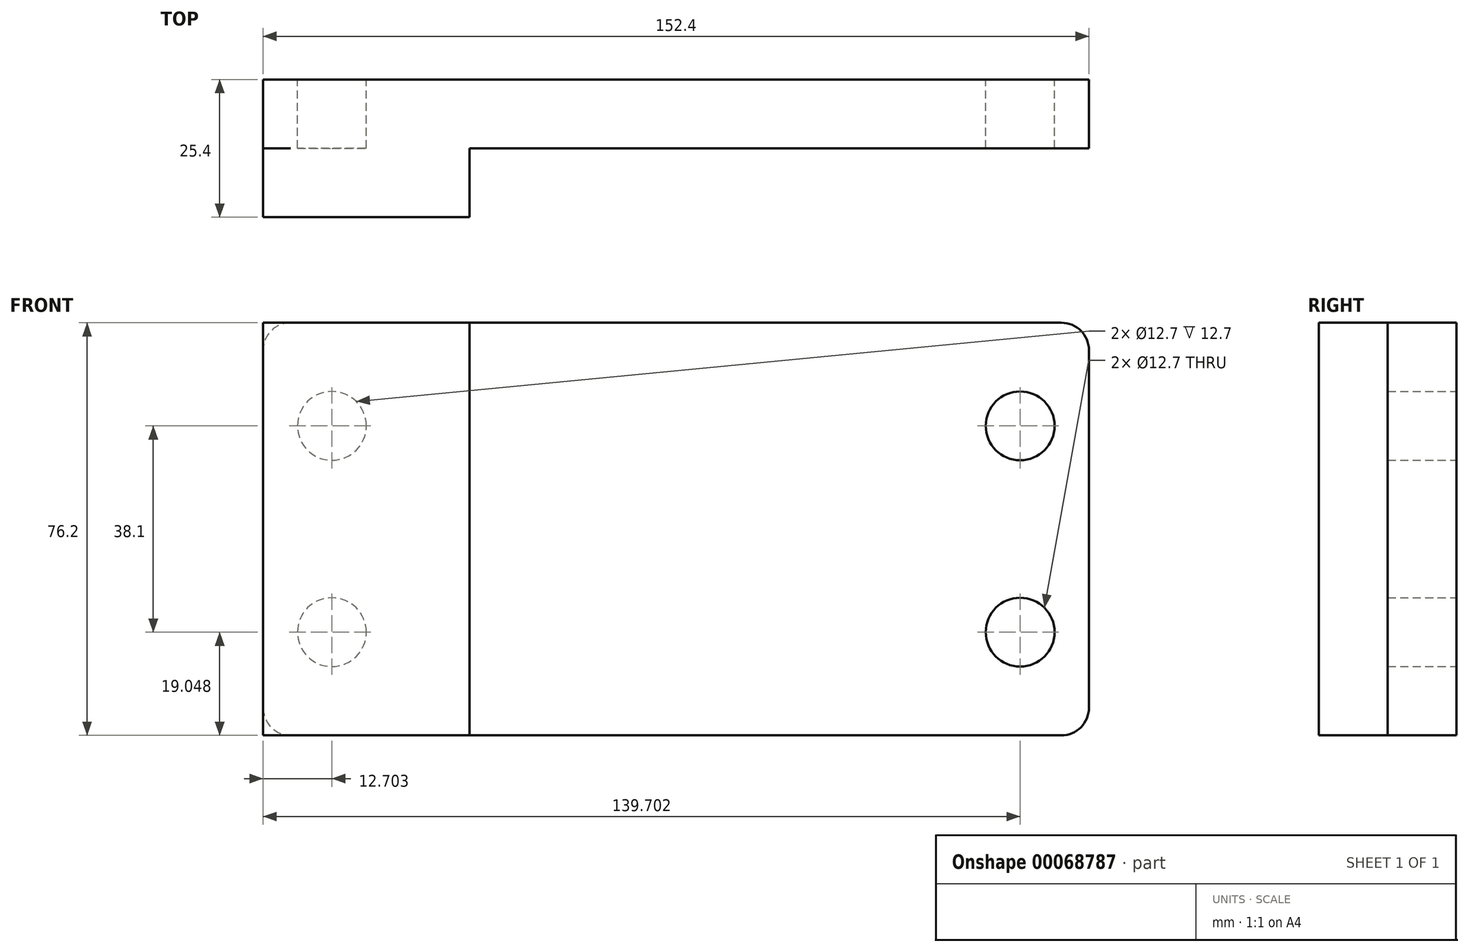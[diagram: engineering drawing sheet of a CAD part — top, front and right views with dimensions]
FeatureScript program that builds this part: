
annotation { "Feature Type Name" : "Feature", "Feature Type Description" : "" }
export const myFeature = defineFeature(function(context is Context, id is Id, definition is map)
    precondition{}
    {
        {
            var Q0;
            Q0=qCreatedBy(makeId("Front.planeOp"),FACE);
            var sketch = newSketch(context, id + "F0", { "sketchPlane" : qUnion([Q0])});
            skLineSegment(sketch, "E0.bottom", {"start": v(-76.72, 31.36) * mm, "end": v(75.68, 31.36) * mm});
            skLineSegment(sketch, "E0.top", {"start": v(-76.72, -44.84) * mm, "end": v(75.68, -44.84) * mm});
            skLineSegment(sketch, "E0.left", {"start": v(-76.72, 31.36) * mm, "end": v(-76.72, -44.84) * mm});
            skLineSegment(sketch, "E0.right", {"start": v(75.68, 31.36) * mm, "end": v(75.68, -44.84) * mm});
            skCircle(sketch, "E1", {"center": v(-64.02, 12.3) * mm, "radius": 6.35 * mm});
            skLineSegment(sketch, "E2.MirrorCS", {"start": v(76.72, 31.36) * mm, "end": v(76.72, -44.84) * mm});
            skLineSegment(sketch, "E3", {"start": v(-0.52, 31.36) * mm, "end": v(-0.52, -44.84) * mm, "construction": true});
            skCircle(sketch, "E4.MirrorC", {"center": v(62.98, 12.3) * mm, "radius": 6.35 * mm});
            skLineSegment(sketch, "E5", {"start": v(-76.72, -6.74) * mm, "end": v(75.68, -6.74) * mm, "construction": true});
            skCircle(sketch, "E6.MirrorC", {"center": v(62.98, -25.8) * mm, "radius": 6.35 * mm});
            skCircle(sketch, "E7.MirrorC", {"center": v(-64.02, -25.8) * mm, "radius": 6.35 * mm});
            skSolve(sketch);
        }
        {
            var Q0;
            Q0=makeQuery(id+"F0.imprint","IMPRINT",FACE,{"disambiguationData":[TD([[makeQuery(id+"F0.imprint","IMPRINT",EDGE,{"derivedFrom":sQuery(id+"F0.wireOp",EDGE,"E0.bottom")}),-1.0]])]});
            extrude(context, id + "F1", {"entities" : qUnion([Q0]), "depth" : 12.7 * mm});
        }
        {
            var Q0;
            Q0=makeQuery(id+"F1.opExtrude","SWEPT_EDGE",EDGE,{"disambiguationData":[OSD([sQuery(id+"F0.wireOp",EDGE,"E0.bottom"),sQuery(id+"F0.wireOp",EDGE,"E0.left")])]});
            var Q1;
            Q1=makeQuery(id+"F1.opExtrude","SWEPT_EDGE",EDGE,{"disambiguationData":[OSD([sQuery(id+"F0.wireOp",EDGE,"E0.top"),sQuery(id+"F0.wireOp",EDGE,"E0.left")])]});
            var Q2;
            Q2=makeQuery(id+"F1.opExtrude","SWEPT_EDGE",EDGE,{"disambiguationData":[OSD([sQuery(id+"F0.wireOp",EDGE,"E0.top"),sQuery(id+"F0.wireOp",EDGE,"E0.right")])]});
            var Q3;
            Q3=makeQuery(id+"F1.opExtrude","SWEPT_EDGE",EDGE,{"disambiguationData":[OSD([sQuery(id+"F0.wireOp",EDGE,"E0.bottom"),sQuery(id+"F0.wireOp",EDGE,"E0.right")])]});
            fillet(context, id + "F2", {"entities" : qUnion([Q0, Q1, Q2, Q3]), "radius" : 5.08 * mm, "tangentPropagation" : true, "allowEdgeOverflow" : false});
        }
        {
            var Q0;
            Q0=makeQuery(id+"F1.opExtrude","CAP_FACE",FACE,{"disambiguationData":[OSD([sQuery(id+"F0.wireOp",EDGE,"E0.bottom"),sQuery(id+"F0.wireOp",EDGE,"E0.top"),sQuery(id+"F0.wireOp",EDGE,"E0.left"),sQuery(id+"F0.wireOp",EDGE,"E0.right"),sQuery(id+"F0.wireOp",EDGE,"E1"),sQuery(id+"F0.wireOp",EDGE,"E6.MirrorC"),sQuery(id+"F0.wireOp",EDGE,"E4.MirrorC"),sQuery(id+"F0.wireOp",EDGE,"E7.MirrorC")])],"isStart":false});
            var sketch = newSketch(context, id + "F3", { "sketchPlane" : qUnion([Q0])});
            skLineSegment(sketch, "E8.bottom", {"start": v(-76.72, -44.84) * mm, "end": v(-38.62, -44.84) * mm});
            skLineSegment(sketch, "E8.top", {"start": v(-76.72, 31.36) * mm, "end": v(-38.62, 31.36) * mm});
            skLineSegment(sketch, "E8.left", {"start": v(-76.72, -44.84) * mm, "end": v(-76.72, 31.36) * mm});
            skLineSegment(sketch, "E8.right", {"start": v(-38.62, -44.84) * mm, "end": v(-38.62, 31.36) * mm});
            skSolve(sketch);
        }
        {
            var Q0;
            Q0 = qSketchRegion(id + "F3", true);
            extrude(context, id + "F4", {"entities" : qUnion([Q0]), "operationType" : NewBodyOperationType.ADD, "depth" : 12.7 * mm});
        }
    });
